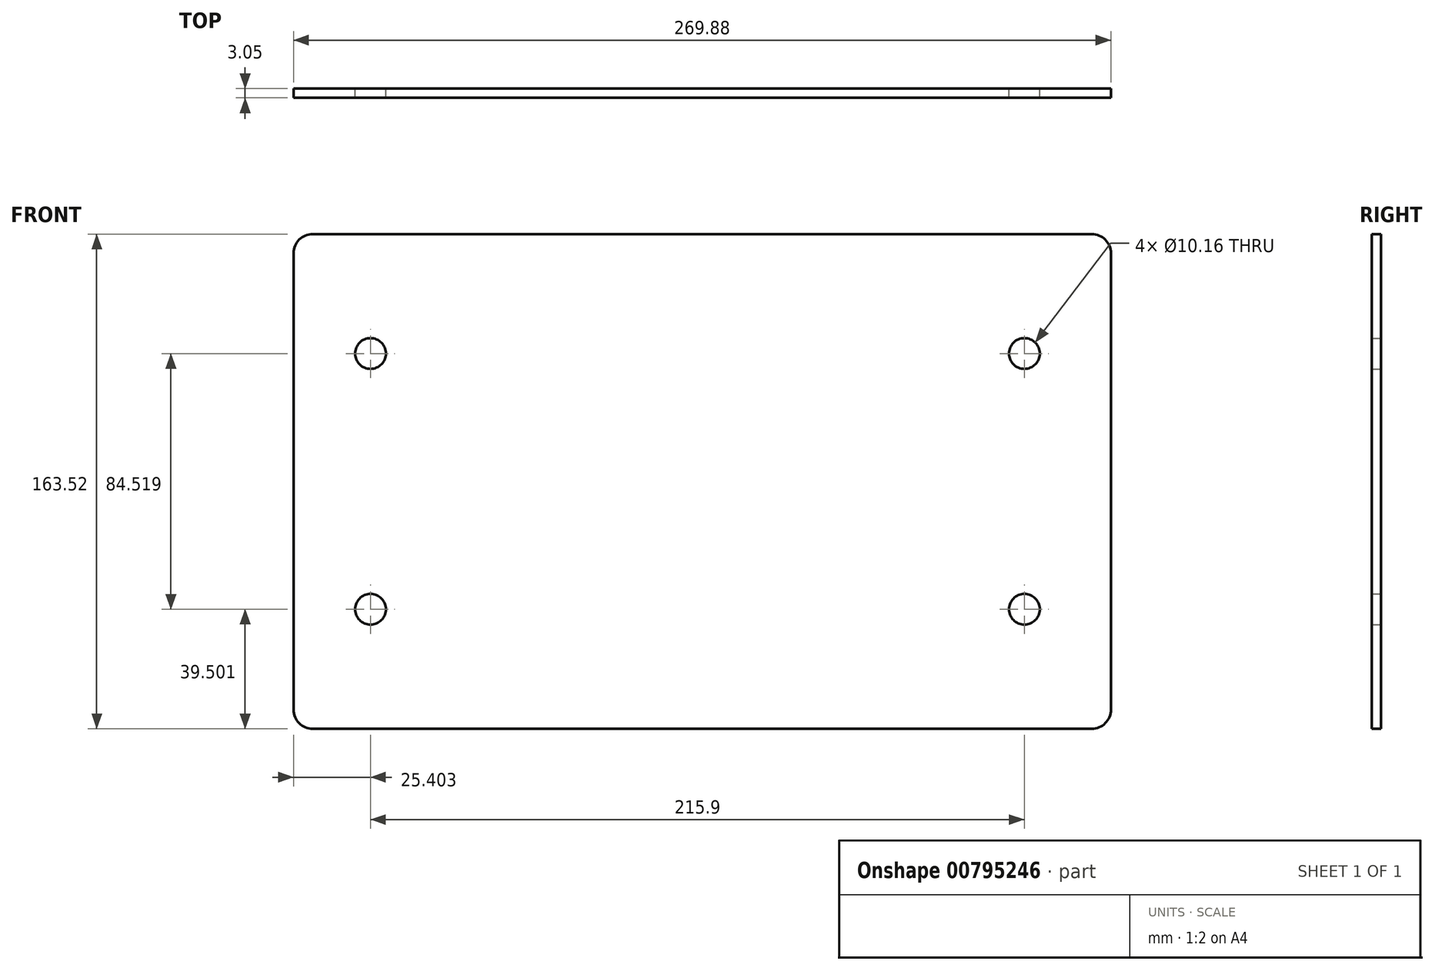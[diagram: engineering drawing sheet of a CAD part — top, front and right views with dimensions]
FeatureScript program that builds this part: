
annotation { "Feature Type Name" : "Feature", "Feature Type Description" : "" }
export const myFeature = defineFeature(function(context is Context, id is Id, definition is map)
    precondition{}
    {
        {
            var Q0;
            Q0=qCreatedBy(makeId("Front.planeOp"),FACE);
            var sketch = newSketch(context, id + "F0", { "sketchPlane" : qUnion([Q0])});
            skLineSegment(sketch, "E0.bottom", {"start": v(-128.59, 81.76) * mm, "end": v(128.59, 81.76) * mm});
            skLineSegment(sketch, "E0.top", {"start": v(-128.59, -81.76) * mm, "end": v(128.59, -81.76) * mm});
            skLineSegment(sketch, "E0.left", {"start": v(-134.94, 75.4) * mm, "end": v(-134.94, -75.4) * mm});
            skLineSegment(sketch, "E0.right", {"start": v(134.94, 75.4) * mm, "end": v(134.94, -75.4) * mm});
            skPoint(sketch, "E0.middle", {"position": v(0, 0) * mm});
            skLineSegment(sketch, "E1.right", {"start": v(-109.54, 64.48) * mm, "end": v(-109.54, 20.03) * mm, "construction": true});
            skLineSegment(sketch, "E2.right", {"start": v(-109.54, -20.03) * mm, "end": v(-109.54, -64.48) * mm, "construction": true});
            skArc(sketch, "E3.0.startCap", {"start": v(-114.62, 64.48) * mm, "mid": v(-109.54, 69.56) * mm, "end": v(-104.46, 64.48) * mm, "construction": true});
            skArc(sketch, "E3.0.endCap", {"start": v(-104.46, 20.03) * mm, "mid": v(-109.54, 14.95) * mm, "end": v(-114.62, 20.03) * mm, "construction": true});
            skLineSegment(sketch, "E3.0.left", {"start": v(-104.46, 64.48) * mm, "end": v(-104.46, 20.03) * mm, "construction": true});
            skLineSegment(sketch, "E3.0.right", {"start": v(-114.62, 64.48) * mm, "end": v(-114.62, 20.03) * mm, "construction": true});
            skArc(sketch, "E3.1.startCap", {"start": v(-114.62, -20.03) * mm, "mid": v(-109.54, -14.95) * mm, "end": v(-104.46, -20.03) * mm, "construction": true});
            skArc(sketch, "E3.1.endCap", {"start": v(-104.46, -64.48) * mm, "mid": v(-109.54, -69.56) * mm, "end": v(-114.62, -64.48) * mm, "construction": true});
            skLineSegment(sketch, "E3.1.left", {"start": v(-104.46, -20.03) * mm, "end": v(-104.46, -64.48) * mm, "construction": true});
            skLineSegment(sketch, "E3.1.right", {"start": v(-114.62, -20.03) * mm, "end": v(-114.62, -64.48) * mm, "construction": true});
            skLineSegment(sketch, "E4", {"start": v(-1.59, 81.76) * mm, "end": v(-1.59, -81.76) * mm, "construction": true});
            skArc(sketch, "E5.MirrorCS", {"start": v(101.28, 20.03) * mm, "mid": v(106.36, 14.95) * mm, "end": v(111.44, 20.03) * mm, "construction": true});
            skLineSegment(sketch, "E6.MirrorCS", {"start": v(101.28, 64.48) * mm, "end": v(101.28, 20.03) * mm, "construction": true});
            skArc(sketch, "E7.MirrorCS", {"start": v(111.44, -20.03) * mm, "mid": v(106.36, -14.95) * mm, "end": v(101.28, -20.03) * mm, "construction": true});
            skLineSegment(sketch, "E8.MirrorCS", {"start": v(101.28, -20.03) * mm, "end": v(101.28, -64.48) * mm, "construction": true});
            skLineSegment(sketch, "E9.MirrorCS", {"start": v(106.36, -20.03) * mm, "end": v(106.36, -64.48) * mm, "construction": true});
            skArc(sketch, "E10.MirrorCS", {"start": v(111.44, 64.48) * mm, "mid": v(106.36, 69.56) * mm, "end": v(101.28, 64.48) * mm, "construction": true});
            skArc(sketch, "E11.MirrorCS", {"start": v(101.28, -64.48) * mm, "mid": v(106.36, -69.56) * mm, "end": v(111.44, -64.48) * mm});
            skLineSegment(sketch, "E12.MirrorCS", {"start": v(111.44, 64.48) * mm, "end": v(111.44, 20.03) * mm, "construction": true});
            skLineSegment(sketch, "E13.MirrorCS", {"start": v(111.44, -20.03) * mm, "end": v(111.44, -64.48) * mm, "construction": true});
            skLineSegment(sketch, "E14.MirrorCS", {"start": v(106.36, 64.48) * mm, "end": v(106.36, 20.03) * mm, "construction": true});
            skPoint(sketch, "E15.visualSharp", {"position": v(-134.94, 81.76) * mm});
            skArc(sketch, "E15.filletArc", {"start": v(-128.59, 81.76) * mm, "mid": v(-133.08, 79.9) * mm, "end": v(-134.94, 75.4) * mm});
            skPoint(sketch, "E16.visualSharp", {"position": v(134.94, 81.76) * mm});
            skArc(sketch, "E16.filletArc", {"start": v(134.94, 75.4) * mm, "mid": v(133.08, 79.9) * mm, "end": v(128.59, 81.76) * mm});
            skPoint(sketch, "E17.visualSharp", {"position": v(134.94, -81.76) * mm});
            skArc(sketch, "E17.filletArc", {"start": v(128.59, -81.76) * mm, "mid": v(133.08, -79.9) * mm, "end": v(134.94, -75.4) * mm});
            skPoint(sketch, "E18.visualSharp", {"position": v(-134.94, -81.76) * mm});
            skArc(sketch, "E18.filletArc", {"start": v(-134.94, -75.4) * mm, "mid": v(-133.08, -79.9) * mm, "end": v(-128.59, -81.76) * mm});
            skCircle(sketch, "E19", {"center": v(-109.54, 42.26) * mm, "radius": 5.08 * mm});
            skCircle(sketch, "E20", {"center": v(-109.54, -42.26) * mm, "radius": 5.08 * mm});
            skCircle(sketch, "E21", {"center": v(106.36, -42.26) * mm, "radius": 5.08 * mm});
            skCircle(sketch, "E22", {"center": v(106.36, 42.26) * mm, "radius": 5.08 * mm});
            skSolve(sketch);
        }
        {
            var Q0;
            Q0 = qSketchRegion(id + "F0", true);
            extrude(context, id + "F1", {"entities" : qUnion([Q0]), "depth" : 3.05 * mm, "offsetDistance" : 25.4 * mm});
        }
    });
